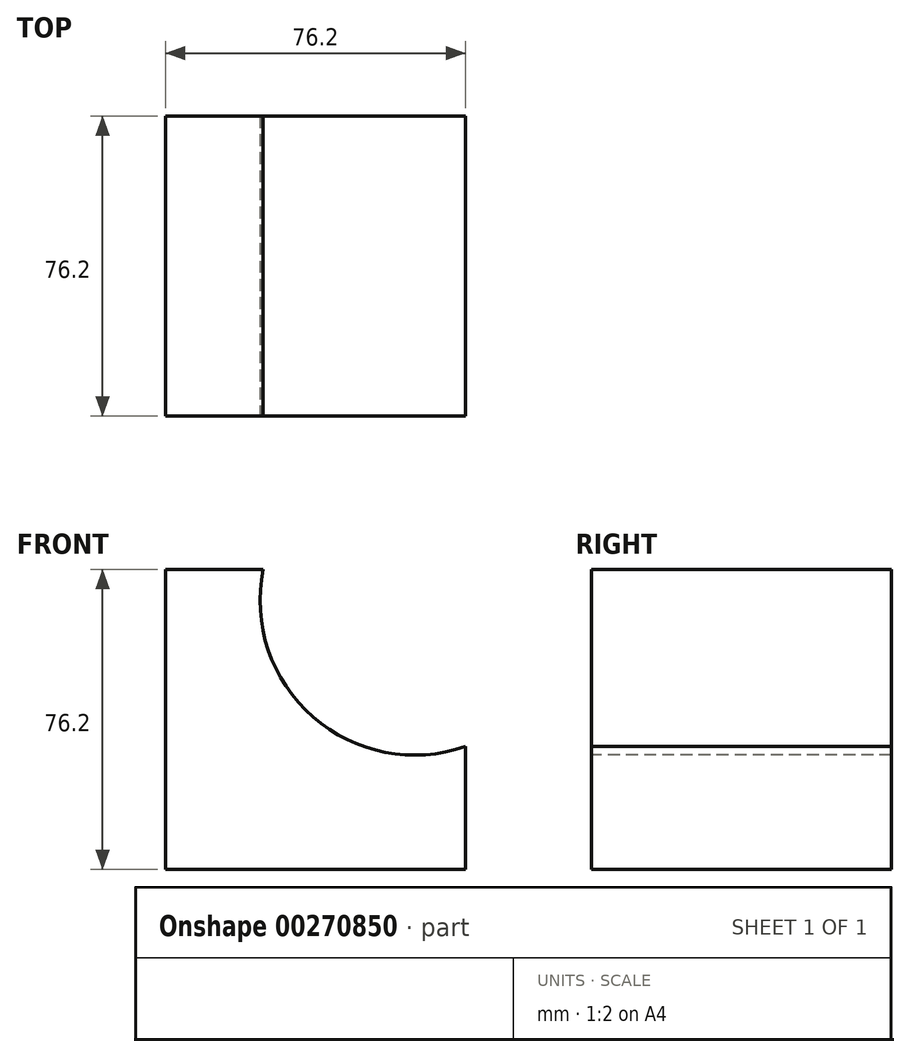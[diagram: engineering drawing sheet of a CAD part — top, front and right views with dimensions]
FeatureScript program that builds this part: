
annotation { "Feature Type Name" : "Feature", "Feature Type Description" : "" }
export const myFeature = defineFeature(function(context is Context, id is Id, definition is map)
    precondition{}
    {
        {
            var Q0;
            Q0=qCreatedBy(makeId("Front.planeOp"),FACE);
            var sketch = newSketch(context, id + "F0", { "sketchPlane" : qUnion([Q0])});
            skLineSegment(sketch, "E0.bottom", {"start": v(-84.41, 86.7) * mm, "end": v(-8.21, 86.7) * mm});
            skLineSegment(sketch, "E0.top", {"start": v(-84.41, 10.5) * mm, "end": v(-8.21, 10.5) * mm});
            skLineSegment(sketch, "E0.left", {"start": v(-84.41, 86.7) * mm, "end": v(-84.41, 10.5) * mm});
            skLineSegment(sketch, "E0.right", {"start": v(-8.21, 86.7) * mm, "end": v(-8.21, 10.5) * mm});
            skSolve(sketch);
        }
        {
            var Q0;
            Q0 = qSketchRegion(id + "F0", true);
            extrude(context, id + "F1", {"entities" : qUnion([Q0]), "depth" : 76.2 * mm});
        }
        {
            var Q0;
            Q0=makeQuery(id+"F1.opExtrude","CAP_FACE",FACE,{"disambiguationData":[OSD([sQuery(id+"F0.wireOp",EDGE,"E0.bottom"),sQuery(id+"F0.wireOp",EDGE,"E0.top"),sQuery(id+"F0.wireOp",EDGE,"E0.left"),sQuery(id+"F0.wireOp",EDGE,"E0.right")])],"isStart":false});
            var sketch = newSketch(context, id + "F2", { "sketchPlane" : qUnion([Q0])});
            skCircle(sketch, "E1", {"center": v(-21.1, 78.85) * mm, "radius": 39.3 * mm});
            skSolve(sketch);
        }
        {
            var Q0;
            {var subQ0=sQuery(id+"F2.wireOp",EDGE,"E1");var subQ1=makeQuery(id+"F1.opExtrude","CAP_EDGE",EDGE,{"disambiguationData":[OSD([sQuery(id+"F0.wireOp",EDGE,"E0.bottom")])],"isStart":false});var subQ2=makeQuery(id+"F2.imprint","INTERSECT",VERTEX,{"derivedFrom":[subQ1,subQ0]});Q0=makeQuery(id+"F2.imprint","IMPRINT",FACE,{"disambiguationData":[TD([[makeQuery(id+"F2.imprint","IMPRINT",EDGE,{"disambiguationData":[TD([[subQ2,-1.0]])],"derivedFrom":subQ0}),1.0]])]});}
            var Q1;
            Q1 = qSketchRegion(id + "F2", true);
            extrude(context, id + "F3", {"entities" : qUnion([Q0, Q1]), "operationType" : NewBodyOperationType.REMOVE, "oppositeDirection" : true, "depth" : 101.6 * mm});
        }
    });
